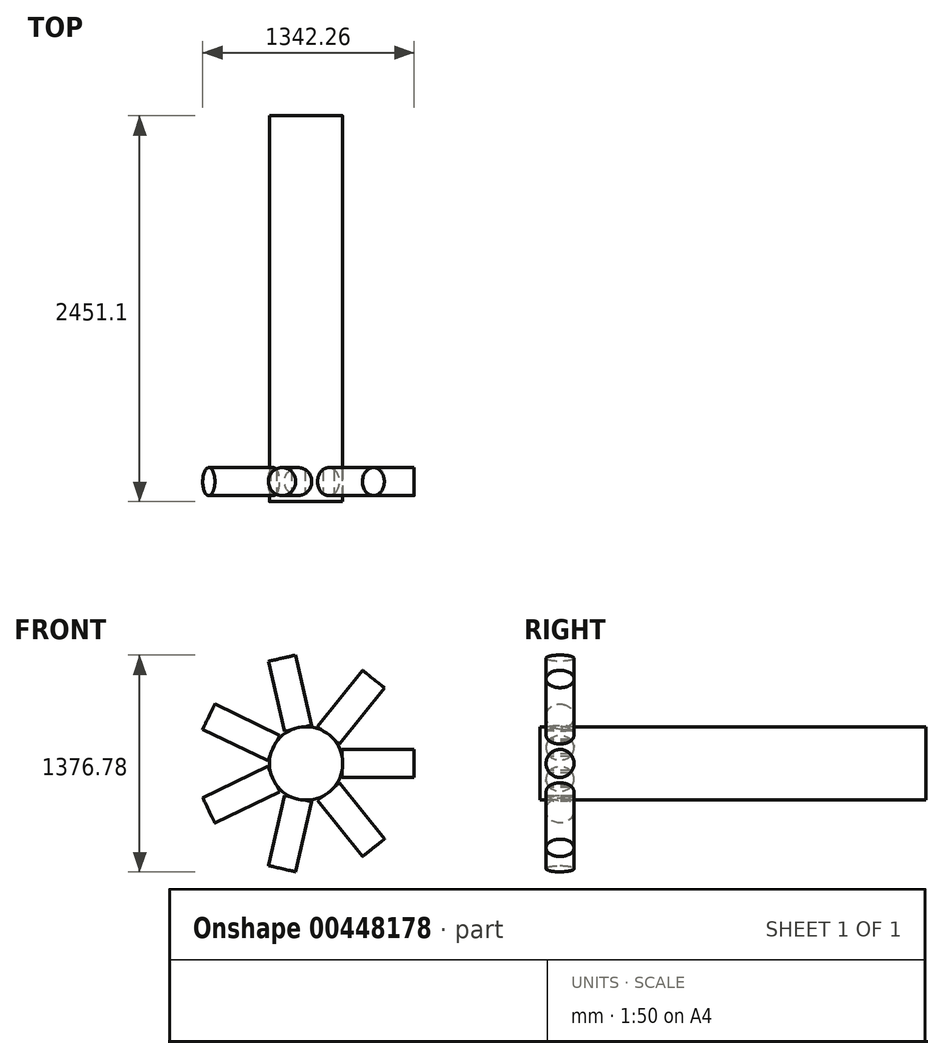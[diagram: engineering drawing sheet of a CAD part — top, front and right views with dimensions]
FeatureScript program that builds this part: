
annotation { "Feature Type Name" : "Feature", "Feature Type Description" : "" }
export const myFeature = defineFeature(function(context is Context, id is Id, definition is map)
    precondition{}
    {
        {
            var Q0;
            Q0=qCreatedBy(makeId("Front.planeOp"),FACE);
            var sketch = newSketch(context, id + "F0", { "sketchPlane" : qUnion([Q0])});
            skCircle(sketch, "E0", {"center": v(0, 0) * mm, "radius": 232.8 * mm});
            skLineSegment(sketch, "E1", {"start": v(0, 0) * mm, "end": v(232.8, 0) * mm});
            skSolve(sketch);
        }
        {
            var Q0;
            Q0=makeQuery(id+"F0.imprint","IMPRINT",FACE,{"disambiguationData":[TD([[makeQuery(id+"F0.imprint","IMPRINT",EDGE,{"derivedFrom":sQuery(id+"F0.wireOp",EDGE,"E0")}),1.0]])]});
            extrude(context, id + "F1", {"entities" : qUnion([Q0]), "oppositeDirection" : true, "depth" : 2451.1 * mm});
        }
        {
            var Q0;
            Q0=qCreatedBy(makeId("Right.planeOp"),FACE);
            cPlane(context, id + "F2", {"entities" : qUnion([Q0]), "cplaneType" : CPlaneType.OFFSET, "offset" : 228.6 * mm, "width" : 152.4 * mm, "height" : 152.4 * mm});
        }
        {
            var Q0;
            Q0=qCreatedBy(id+"F2.planeOp",FACE);
            var sketch = newSketch(context, id + "F3", { "sketchPlane" : qUnion([Q0])});
            skCircle(sketch, "E2", {"center": v(127, 0) * mm, "radius": 88.9 * mm});
            skSolve(sketch);
        }
        {
            var Q0;
            Q0 = qSketchRegion(id + "F3", true);
            extrude(context, id + "F4", {"entities" : qUnion([Q0]), "operationType" : NewBodyOperationType.ADD, "depth" : 457.2 * mm});
        }
        {
            var Q0;
            Q0=makeQuery(id+"F1.opExtrude","SWEPT_BODY",BODY,{"disambiguationData":[OSD([sQuery(id+"F0.wireOp",EDGE,"E0")])]});
            var Q1;
            Q1=makeQuery(id+"F1.opExtrude","SWEPT_FACE",FACE,{"disambiguationData":[OSD([sQuery(id+"F0.wireOp",EDGE,"E0")])]});
            circularPattern(context, id + "F5", {"entities" : qUnion([Q0]), "axis" : qUnion([Q1]), "angle" : 360 * degree, "instanceCount" : 7, "equalSpace" : true});
        }
    });
